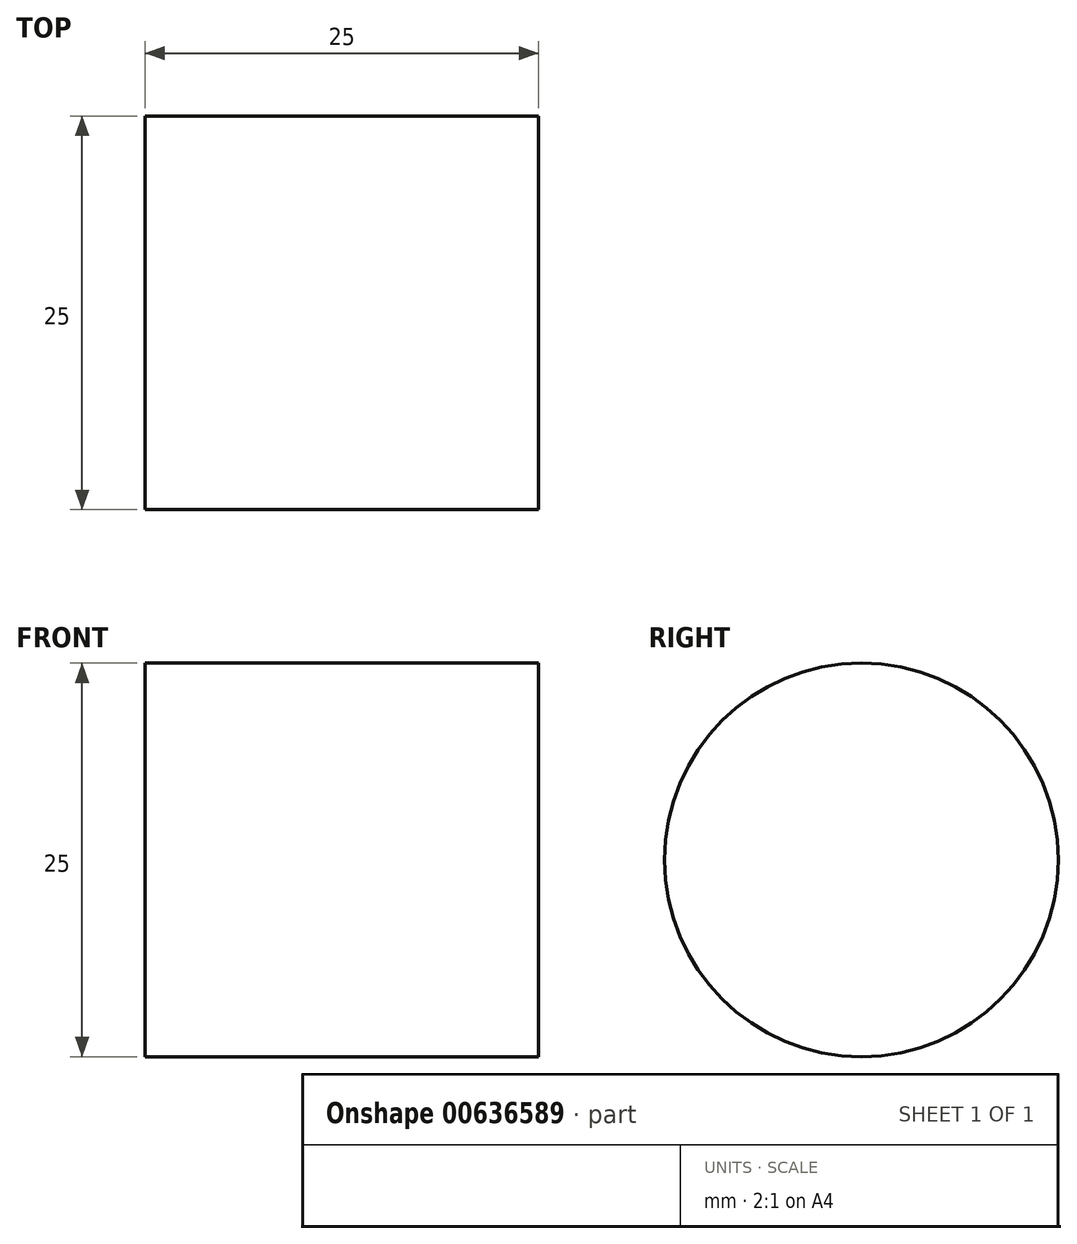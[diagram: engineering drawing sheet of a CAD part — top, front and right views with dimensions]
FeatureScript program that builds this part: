
annotation { "Feature Type Name" : "Feature", "Feature Type Description" : "" }
export const myFeature = defineFeature(function(context is Context, id is Id, definition is map)
    precondition{}
    {
        {
            var Q0;
            Q0=qCreatedBy(makeId("Right.planeOp"),FACE);
            var sketch = newSketch(context, id + "F0", { "sketchPlane" : qUnion([Q0])});
            skCircle(sketch, "E0", {"center": v(0, 0) * mm, "radius": 12.5 * mm});
            skSolve(sketch);
        }
        {
            var Q0;
            Q0=makeQuery(id+"F0.imprint","IMPRINT",FACE,{"disambiguationData":[TD([[makeQuery(id+"F0.imprint","IMPRINT",EDGE,{"derivedFrom":sQuery(id+"F0.wireOp",EDGE,"E0")}),1.0]])]});
            extrude(context, id + "F1", {"entities" : qUnion([Q0]), "depth" : 25 * mm, "offsetDistance" : 25 * mm});
        }
    });
